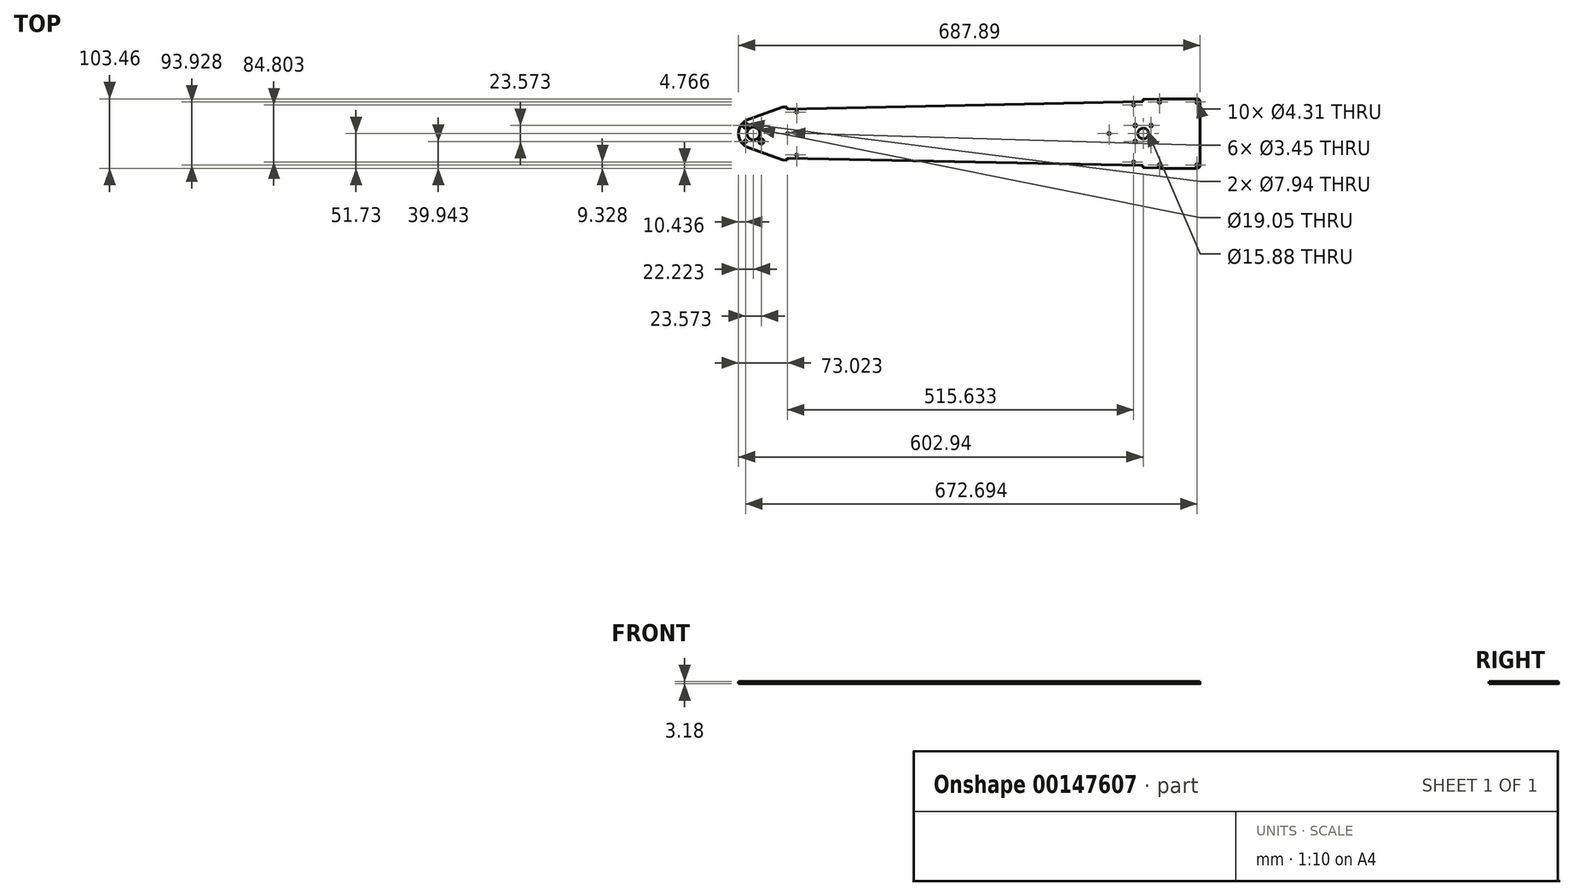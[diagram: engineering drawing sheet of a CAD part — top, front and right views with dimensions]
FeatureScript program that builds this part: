
annotation { "Feature Type Name" : "Feature", "Feature Type Description" : "" }
export const myFeature = defineFeature(function(context is Context, id is Id, definition is map)
    precondition{}
    {
        {
            var Q0;
            Q0=qCreatedBy(makeId("Top.planeOp"),FACE);
            var sketch = newSketch(context, id + "F0", { "sketchPlane" : qUnion([Q0])});
            skPoint(sketch, "E0.rect.middle", {"position": v(0, 0) * mm});
            skCircle(sketch, "E1", {"center": v(0, 0) * mm, "radius": 7.94 * mm});
            skLineSegment(sketch, "E2.bottom", {"start": v(11.79, 11.79) * mm, "end": v(-11.79, 11.79) * mm, "construction": true});
            skLineSegment(sketch, "E2.left", {"start": v(11.79, 11.79) * mm, "end": v(11.79, -11.79) * mm, "construction": true});
            skLineSegment(sketch, "E2.right", {"start": v(-11.79, 11.79) * mm, "end": v(-11.79, -11.79) * mm, "construction": true});
            skCircle(sketch, "E3", {"center": v(-11.79, 11.79) * mm, "radius": 2.15 * mm});
            skCircle(sketch, "E4", {"center": v(11.79, 11.79) * mm, "radius": 2.15 * mm});
            skCircle(sketch, "E5", {"center": v(11.79, -11.79) * mm, "radius": 2.15 * mm});
            skCircle(sketch, "E6", {"center": v(-11.79, -11.79) * mm, "radius": 2.15 * mm});
            skArc(sketch, "E7", {"start": v(-588.32, 20.88) * mm, "mid": v(-602.94, 0) * mm, "end": v(-588.32, -20.88) * mm});
            skLineSegment(sketch, "E8.bottom", {"start": v(-592.5, 11.79) * mm, "end": v(-568.93, 11.79) * mm, "construction": true});
            skLineSegment(sketch, "E8.top", {"start": v(-592.5, -11.79) * mm, "end": v(-568.93, -11.79) * mm, "construction": true});
            skLineSegment(sketch, "E8.left", {"start": v(-592.5, 11.79) * mm, "end": v(-592.5, -11.79) * mm, "construction": true});
            skLineSegment(sketch, "E8.right", {"start": v(-568.93, 11.79) * mm, "end": v(-568.93, -11.79) * mm, "construction": true});
            skCircle(sketch, "E9", {"center": v(-568.93, 11.79) * mm, "radius": 2.15 * mm});
            skCircle(sketch, "E10", {"center": v(-580.72, 0) * mm, "radius": 9.53 * mm});
            skCircle(sketch, "E11", {"center": v(-592.5, 11.79) * mm, "radius": 3.97 * mm});
            skCircle(sketch, "E12", {"center": v(-592.5, -11.79) * mm, "radius": 2.15 * mm});
            skCircle(sketch, "E13", {"center": v(-568.93, -11.79) * mm, "radius": 3.97 * mm});
            skLineSegment(sketch, "E14", {"start": v(0, 0) * mm, "end": v(-580.72, 0) * mm, "construction": true});
            skLineSegment(sketch, "E15", {"start": v(-588.32, -20.88) * mm, "end": v(-537.06, -39.54) * mm});
            skLineSegment(sketch, "E16", {"start": v(-588.32, 20.88) * mm, "end": v(-537.06, 39.54) * mm});
            skLineSegment(sketch, "E17", {"start": v(-530.65, -36.5) * mm, "end": v(-0.1, -47.46) * mm});
            skLineSegment(sketch, "E18", {"start": v(-530.65, 36.5) * mm, "end": v(-0.1, 47.46) * mm});
            skLineSegment(sketch, "E19", {"start": v(-530.72, 39.67) * mm, "end": v(-530.65, 36.5) * mm});
            skLineSegment(sketch, "E20", {"start": v(-530.72, 39.67) * mm, "end": v(-537.06, 39.54) * mm});
            skLineSegment(sketch, "E21", {"start": v(-530.65, -36.5) * mm, "end": v(-530.72, -39.67) * mm});
            skLineSegment(sketch, "E22", {"start": v(-530.72, -39.67) * mm, "end": v(-537.06, -39.54) * mm});
            skLineSegment(sketch, "E23", {"start": v(-0.1, -47.46) * mm, "end": v(-0.16, -50.63) * mm});
            skLineSegment(sketch, "E24", {"start": v(-0.1, 47.46) * mm, "end": v(-0.16, 50.63) * mm});
            skLineSegment(sketch, "E25", {"start": v(-530.65, 36.5) * mm, "end": v(-530.55, 31.74) * mm, "construction": true});
            skLineSegment(sketch, "E26", {"start": v(-530.55, 31.74) * mm, "end": v(-516.27, 32.03) * mm, "construction": true});
            skLineSegment(sketch, "E27", {"start": v(-530.65, -36.5) * mm, "end": v(-530.55, -31.74) * mm, "construction": true});
            skLineSegment(sketch, "E28", {"start": v(-0.1, -47.46) * mm, "end": v(0, -42.7) * mm, "construction": true});
            skLineSegment(sketch, "E29", {"start": v(0, -42.7) * mm, "end": v(-14.28, -42.4) * mm, "construction": true});
            skLineSegment(sketch, "E30", {"start": v(-0.1, 47.46) * mm, "end": v(0, 42.7) * mm, "construction": true});
            skLineSegment(sketch, "E31", {"start": v(0, 42.7) * mm, "end": v(-14.28, 42.4) * mm, "construction": true});
            skCircle(sketch, "E32", {"center": v(-516.27, 32.03) * mm, "radius": 1.73 * mm});
            skCircle(sketch, "E33", {"center": v(-14.28, 42.4) * mm, "radius": 1.73 * mm});
            skCircle(sketch, "E34", {"center": v(-14.28, -42.4) * mm, "radius": 1.73 * mm});
            skCircle(sketch, "E35", {"center": v(-516.27, -32.03) * mm, "radius": 1.73 * mm});
            skLineSegment(sketch, "E36", {"start": v(-11.79, -11.79) * mm, "end": v(11.79, -11.79) * mm, "construction": true});
            skLineSegment(sketch, "E37", {"start": v(-568.93, 11.79) * mm, "end": v(-529.92, 11.79) * mm, "construction": true});
            skLineSegment(sketch, "E38", {"start": v(-529.92, 11.79) * mm, "end": v(-529.92, 0) * mm, "construction": true});
            skLineSegment(sketch, "E39", {"start": v(-11.79, 11.79) * mm, "end": v(-50.8, 11.79) * mm, "construction": true});
            skLineSegment(sketch, "E40", {"start": v(-50.8, 11.79) * mm, "end": v(-50.8, 0) * mm, "construction": true});
            skCircle(sketch, "E41", {"center": v(-529.92, 0) * mm, "radius": 1.73 * mm});
            skCircle(sketch, "E42", {"center": v(-50.8, 0) * mm, "radius": 1.73 * mm});
            skLineSegment(sketch, "E43", {"start": v(0, 0) * mm, "end": v(84.95, 0) * mm, "construction": true});
            skLineSegment(sketch, "E44", {"start": v(84.95, 0) * mm, "end": v(84.95, 0) * mm});
            skCircle(sketch, "E45", {"center": v(24.51, 46.96) * mm, "radius": 2.15 * mm});
            skArc(sketch, "E46", {"start": v(24.51, 51.73) * mm, "mid": v(24.4, 51.73) * mm, "end": v(24.3, 51.72) * mm});
            skLineSegment(sketch, "E47", {"start": v(24.51, 51.73) * mm, "end": v(84.95, 51.73) * mm});
            skLineSegment(sketch, "E48", {"start": v(84.95, 51.73) * mm, "end": v(84.95, -51.73) * mm});
            skLineSegment(sketch, "E49", {"start": v(84.95, -51.73) * mm, "end": v(24.51, -51.73) * mm});
            skArc(sketch, "E50", {"start": v(24.3, -51.72) * mm, "mid": v(24.4, -51.73) * mm, "end": v(24.51, -51.73) * mm});
            skLineSegment(sketch, "E51.bottom", {"start": v(24.51, 46.96) * mm, "end": v(80.2, 46.96) * mm, "construction": true});
            skLineSegment(sketch, "E51.top", {"start": v(24.51, -46.96) * mm, "end": v(80.2, -46.96) * mm, "construction": true});
            skLineSegment(sketch, "E51.left", {"start": v(24.51, 46.96) * mm, "end": v(24.51, -46.96) * mm, "construction": true});
            skLineSegment(sketch, "E51.right", {"start": v(80.2, 46.96) * mm, "end": v(80.2, -46.96) * mm, "construction": true});
            skPoint(sketch, "E51.middle", {"position": v(52.35, 0) * mm});
            skLineSegment(sketch, "E52", {"start": v(80.2, 46.96) * mm, "end": v(80.2, 51.73) * mm, "construction": true});
            skLineSegment(sketch, "E53", {"start": v(80.2, 46.96) * mm, "end": v(84.95, 46.96) * mm, "construction": true});
            skLineSegment(sketch, "E54", {"start": v(24.51, 46.96) * mm, "end": v(24.51, 51.73) * mm, "construction": true});
            skCircle(sketch, "E55", {"center": v(80.2, 46.96) * mm, "radius": 2.15 * mm});
            skCircle(sketch, "E56", {"center": v(80.2, -46.96) * mm, "radius": 2.15 * mm});
            skCircle(sketch, "E57", {"center": v(24.51, -46.96) * mm, "radius": 2.15 * mm});
            skLineSegment(sketch, "E58", {"start": v(-588.32, -20.88) * mm, "end": v(-562.7, -20.88) * mm, "construction": true});
            skLineSegment(sketch, "E59", {"start": v(-562.7, -20.88) * mm, "end": v(-562.7, -30.21) * mm, "construction": true});
            skLineSegment(sketch, "E60", {"start": v(-588.32, -20.88) * mm, "end": v(-588.32, 20.88) * mm, "construction": true});
            skLineSegment(sketch, "E61", {"start": v(-592.5, 0) * mm, "end": v(-588.32, 0) * mm, "construction": true});
            skLineSegment(sketch, "E62", {"start": v(-530.55, -31.74) * mm, "end": v(-516.27, -32.03) * mm, "construction": true});
            skLineSegment(sketch, "E63", {"start": v(24.3, 51.72) * mm, "end": v(-0.16, 50.63) * mm});
            skLineSegment(sketch, "E64", {"start": v(-0.16, -50.63) * mm, "end": v(24.3, -51.72) * mm});
            skPoint(sketch, "E65.endSnap0", {"position": v(0, 11.79) * mm});
            skLineSegment(sketch, "E66", {"start": v(52.35, -46.96) * mm, "end": v(52.35, -26.32) * mm, "construction": true});
            skCircle(sketch, "E67", {"center": v(52.35, -26.32) * mm, "radius": 11.28 * mm, "construction": true});
            skCircle(sketch, "E68", {"center": v(-580.72, 0) * mm, "radius": 24.52 * mm, "construction": true});
            skLineSegment(sketch, "E69", {"start": v(-581.22, -24.51) * mm, "end": v(52.35, -37.6) * mm, "construction": true});
            skLineSegment(sketch, "E70", {"start": v(-264.44, -31.06) * mm, "end": v(-264.66, -42) * mm, "construction": true});
            skLineSegment(sketch, "E71", {"start": v(-264.44, -31.06) * mm, "end": v(-264.44, 0) * mm, "construction": true});
            skLineSegment(sketch, "E72", {"start": v(-264.44, 0) * mm, "end": v(-264.44, 31.06) * mm, "construction": true});
            skLineSegment(sketch, "E73", {"start": v(-264.44, 31.06) * mm, "end": v(-264.66, 42) * mm, "construction": true});
            skLineSegment(sketch, "E74", {"start": v(0, 42.7) * mm, "end": v(0, -42.7) * mm, "construction": true});
            skSolve(sketch);
        }
        {
            var Q0;
            Q0=qSketchRegion(id+"F0",true);
            extrude(context, id + "F1", {"entities" : qUnion([Q0]), "depth" : 3.17 * mm});
        }
        {
            var Q0;
            Q0=makeQuery(id+"F1.opExtrude","SWEPT_EDGE",EDGE,{"disambiguationData":[OSD([sQuery(id+"F0.wireOp",EDGE,"E47"),sQuery(id+"F0.wireOp",EDGE,"E48")])]});
            var Q1;
            Q1=makeQuery(id+"F1.opExtrude","SWEPT_EDGE",EDGE,{"disambiguationData":[OSD([sQuery(id+"F0.wireOp",EDGE,"E48"),sQuery(id+"F0.wireOp",EDGE,"E49")])]});
            fillet(context, id + "F2", {"entities" : qUnion([Q0, Q1]), "radius" : 4.76 * mm, "tangentPropagation" : true, "allowEdgeOverflow" : false});
        }
    });
